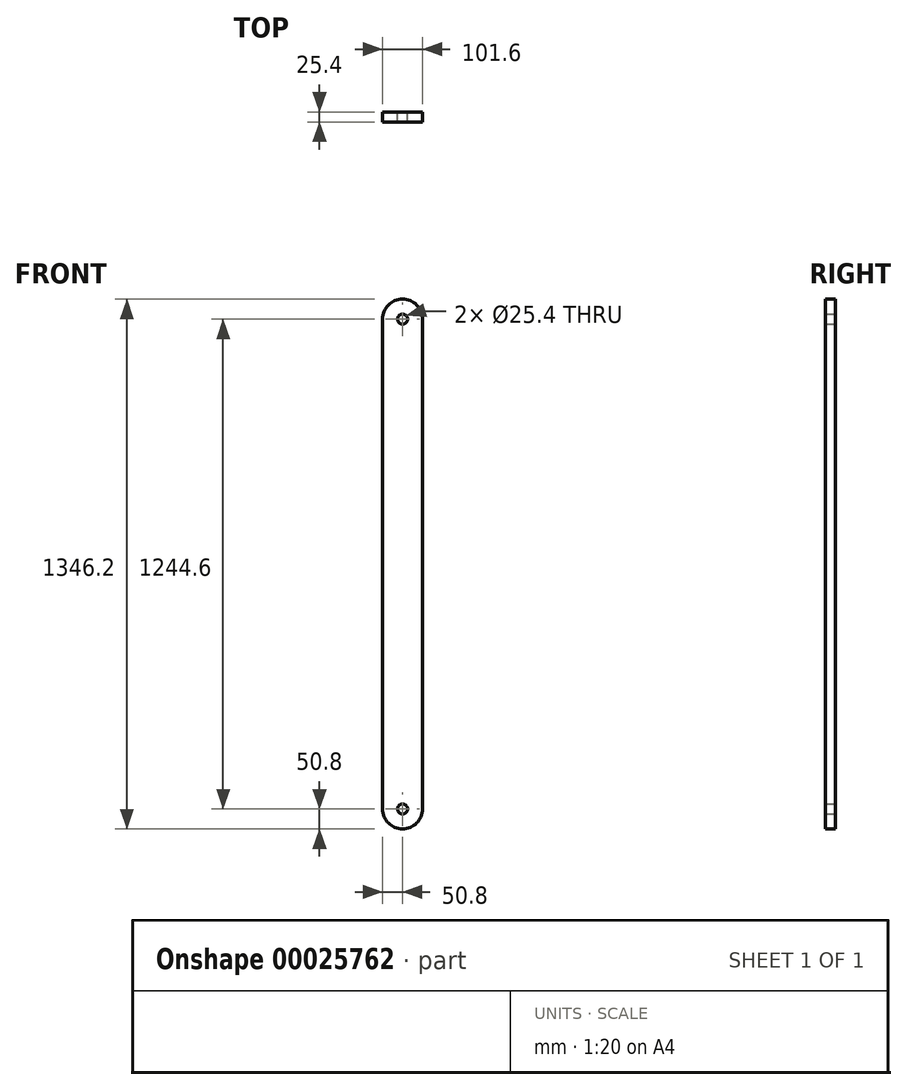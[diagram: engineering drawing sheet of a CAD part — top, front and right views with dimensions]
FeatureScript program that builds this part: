
annotation { "Feature Type Name" : "Feature", "Feature Type Description" : "" }
export const myFeature = defineFeature(function(context is Context, id is Id, definition is map)
    precondition{}
    {
        {
            var Q0;
            Q0=qCreatedBy(makeId("Front.planeOp"),FACE);
            var sketch = newSketch(context, id + "F0", { "sketchPlane" : qUnion([Q0])});
            skCircle(sketch, "E0", {"center": v(0, 0) * mm, "radius": 12.7 * mm});
            skLineSegment(sketch, "E1", {"start": v(50.8, 0) * mm, "end": v(50.8, 1244.6) * mm});
            skLineSegment(sketch, "E2", {"start": v(-50.8, 0) * mm, "end": v(-50.8, 1244.6) * mm});
            skArc(sketch, "E3", {"start": v(-50.8, 0) * mm, "mid": v(0, -50.8) * mm, "end": v(50.8, 0) * mm});
            skArc(sketch, "E4", {"start": v(50.8, 1244.6) * mm, "mid": v(0, 1295.4) * mm, "end": v(-50.8, 1244.6) * mm});
            skCircle(sketch, "E5", {"center": v(0, 1244.6) * mm, "radius": 12.7 * mm});
            skSolve(sketch);
        }
        {
            var Q0;
            Q0=qSketchRegion(id+"F0",true);
            extrude(context, id + "F1", {"entities" : qUnion([Q0]), "depth" : 25.4 * mm});
        }
    });
